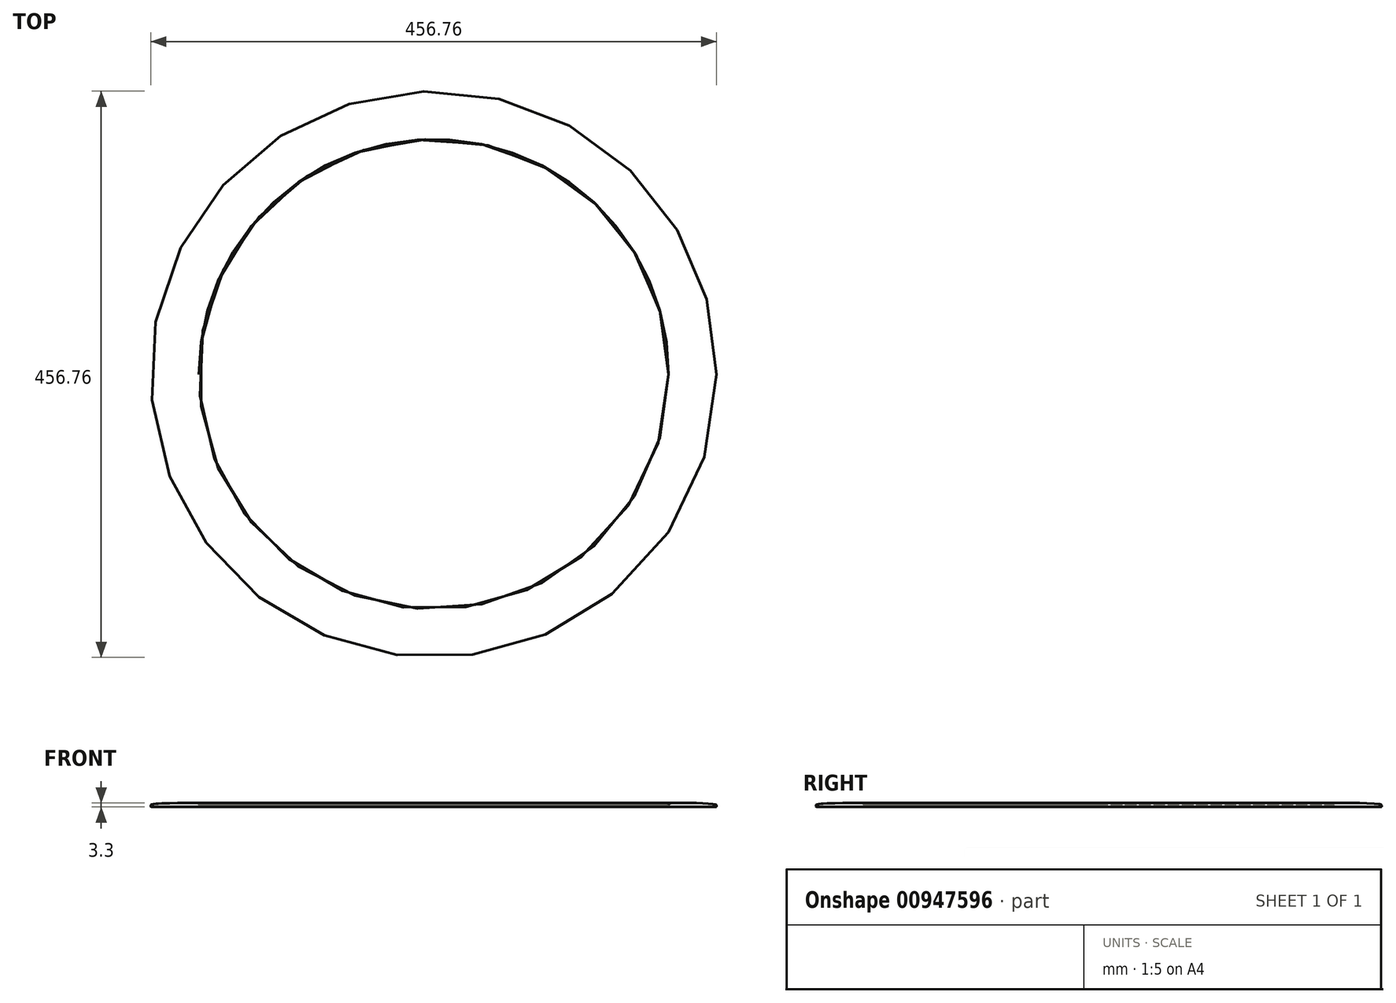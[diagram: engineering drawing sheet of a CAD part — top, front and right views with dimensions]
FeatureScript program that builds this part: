
annotation { "Feature Type Name" : "Feature", "Feature Type Description" : "" }
export const myFeature = defineFeature(function(context is Context, id is Id, definition is map)
    precondition{}
    {
        {
            var Q0;
            Q0=qCreatedBy(makeId("Front.planeOp"),FACE);
            var sketch = newSketch(context, id + "F0", { "sketchPlane" : qUnion([Q0])});
            skLineSegment(sketch, "E0", {"start": v(0, 0) * mm, "end": v(0, 158.75) * mm, "construction": true});
            skLineSegment(sketch, "E1", {"start": v(0, 0) * mm, "end": v(228.6, 0) * mm, "construction": true});
            skLineSegment(sketch, "E2", {"start": v(0, 158.75) * mm, "end": v(44.45, 158.75) * mm, "construction": true});
            skLineSegment(sketch, "E3", {"start": v(44.45, 158.75) * mm, "end": v(44.45, 143.35) * mm, "construction": true});
            skLineSegment(sketch, "E4", {"start": v(44.45, 158.75) * mm, "end": v(86, 158.75) * mm, "construction": true});
            skFitSpline(sketch, "E5", {"points": [v(86, 158.75) * mm, v(63.64, 148.01) * mm, v(44.45, 120.75) * mm, v(41.2, 74.17) * mm, v(59.88, 37.7) * mm, v(85.33, 18.53) * mm, v(127.5, 6.62) * mm, v(179.12, 3.65) * mm, v(188.03, 3.3) * mm, v(189.18, 2.94) * mm, v(189.55, 2.35) * mm, v(189.64, 2) * mm, v(188.74, 0) * mm], "startDerivative": vector(-219.08, -34.84) * mm, "endDerivative": vector(-71.32, -16.42) * mm});
            skPoint(sketch, "E6", {"position": v(65.23, 158.75) * mm});
            skFitSpline(sketch, "E7.MirrorCS", {"points": [v(-86, 158.75) * mm, v(-63.64, 148.01) * mm, v(-44.45, 120.75) * mm, v(-41.2, 74.17) * mm, v(-59.88, 37.7) * mm, v(-85.33, 18.53) * mm, v(-127.5, 6.62) * mm, v(-179.12, 3.65) * mm, v(-188.03, 3.3) * mm, v(-189.18, 2.94) * mm, v(-189.55, 2.35) * mm, v(-189.64, 2) * mm, v(-188.74, 0) * mm], "startDerivative": vector(219.08, -34.84) * mm, "endDerivative": vector(71.32, -16.42) * mm});
            skCircle(sketch, "E8", {"center": v(592.28, -587.42) * mm, "radius": 79.38 * mm});
            skFitSpline(sketch, "E9", {"points": [v(188.74, 0) * mm, v(142.2, 1) * mm, v(105.49, 6.94) * mm, v(70.12, 22.81) * mm, v(43.63, 55.57) * mm, v(36.1, 94.48) * mm, v(44.5, 129.14) * mm, v(58.85, 148.13) * mm, v(71.22, 156.88) * mm, v(74.26, 158.75) * mm, v(74.26, 158.75) * mm, v(86, 158.75) * mm], "startDerivative": vector(-370.06, -4.92) * mm, "endDerivative": vector(-42.57, -70.86) * mm});
            skLineSegment(sketch, "E10", {"start": v(53.68, 142.98) * mm, "end": v(56.49, 141.19) * mm});
            skFitSpline(sketch, "E11", {"points": [v(189.62, 1.7) * mm, v(189.8, 0.43) * mm, v(191.06, 0) * mm, v(226.52, 0) * mm, v(228.35, 0.14) * mm, v(228.38, 0.37) * mm, v(228.32, 1.15) * mm, v(227.18, 2) * mm, v(192.18, 3.05) * mm, v(190.01, 2.53) * mm, v(189.62, 1.7) * mm]});
            skSolve(sketch);
        }
        {
            var Q0;
            Q0=makeQuery(id+"F0.imprint","IMPRINT",FACE,{"disambiguationData":[TD([[makeQuery(id+"F0.imprint","IMPRINT",EDGE,{"derivedFrom":sQuery(id+"F0.wireOp",EDGE,"E5")}),-1.0]])]});
            var Q1;
            Q1=sQuery(id+"F0.wireOp",EDGE,"E0");
            revolve(context, id + "F1", {"surfaceOperationType" : NewSurfaceOperationType.NEW, "entities" : qUnion([Q0]), "axis" : qUnion([Q1]), "revolveType" : RevolveType.FULL});
        }
        {
            var Q0;
            {var subQ0=sQuery(id+"F0.wireOp",EDGE,"E11");var subQ1=sQuery(id+"F0.wireOp",EDGE,"E5");var subQ2=makeQuery(id+"F0.imprint","INTERSECT",VERTEX,{"disambiguationData":[OD(0.0)],"derivedFrom":[subQ1,subQ0]});Q0=makeQuery(id+"F0.imprint","IMPRINT",FACE,{"disambiguationData":[TD([[makeQuery(id+"F0.imprint","IMPRINT",EDGE,{"disambiguationData":[TD([[subQ2,-1.0]])],"derivedFrom":subQ1}),1.0]])]});}
            var Q1;
            {var subQ0=sQuery(id+"F0.wireOp",EDGE,"E5");Q1=makeQuery(id+"F1.opRevolve","SWEPT_FACE",FACE,{"disambiguationData":[OSD([subQ0]),TDD([makeQuery(id+"F0.imprint","IMPRINT",EDGE,{"disambiguationData":[TD([[makeQuery(id+"F0.imprint","INTERSECT",VERTEX,{"derivedFrom":[subQ0,sQuery(id+"F0.wireOp",EDGE,"E10")]}),-1.0]])],"derivedFrom":subQ0})])]});}
            revolve(context, id + "F2", {"surfaceOperationType" : NewSurfaceOperationType.NEW, "entities" : qUnion([Q0]), "axis" : qUnion([Q1]), "revolveType" : RevolveType.FULL});
        }
        {
            var Q0;
            Q0=makeQuery(id+"F1.opRevolve","SWEPT_BODY",BODY,{"disambiguationData":[OSD([sQuery(id+"F0.wireOp",EDGE,"E5"),sQuery(id+"F0.wireOp",EDGE,"E9"),sQuery(id+"F0.wireOp",EDGE,"E10"),sQuery(id+"F0.wireOp",EDGE,"E11")])]});
            deleteBodies(context, id + "F3", {"entities" : qUnion([Q0])});
        }
    });
